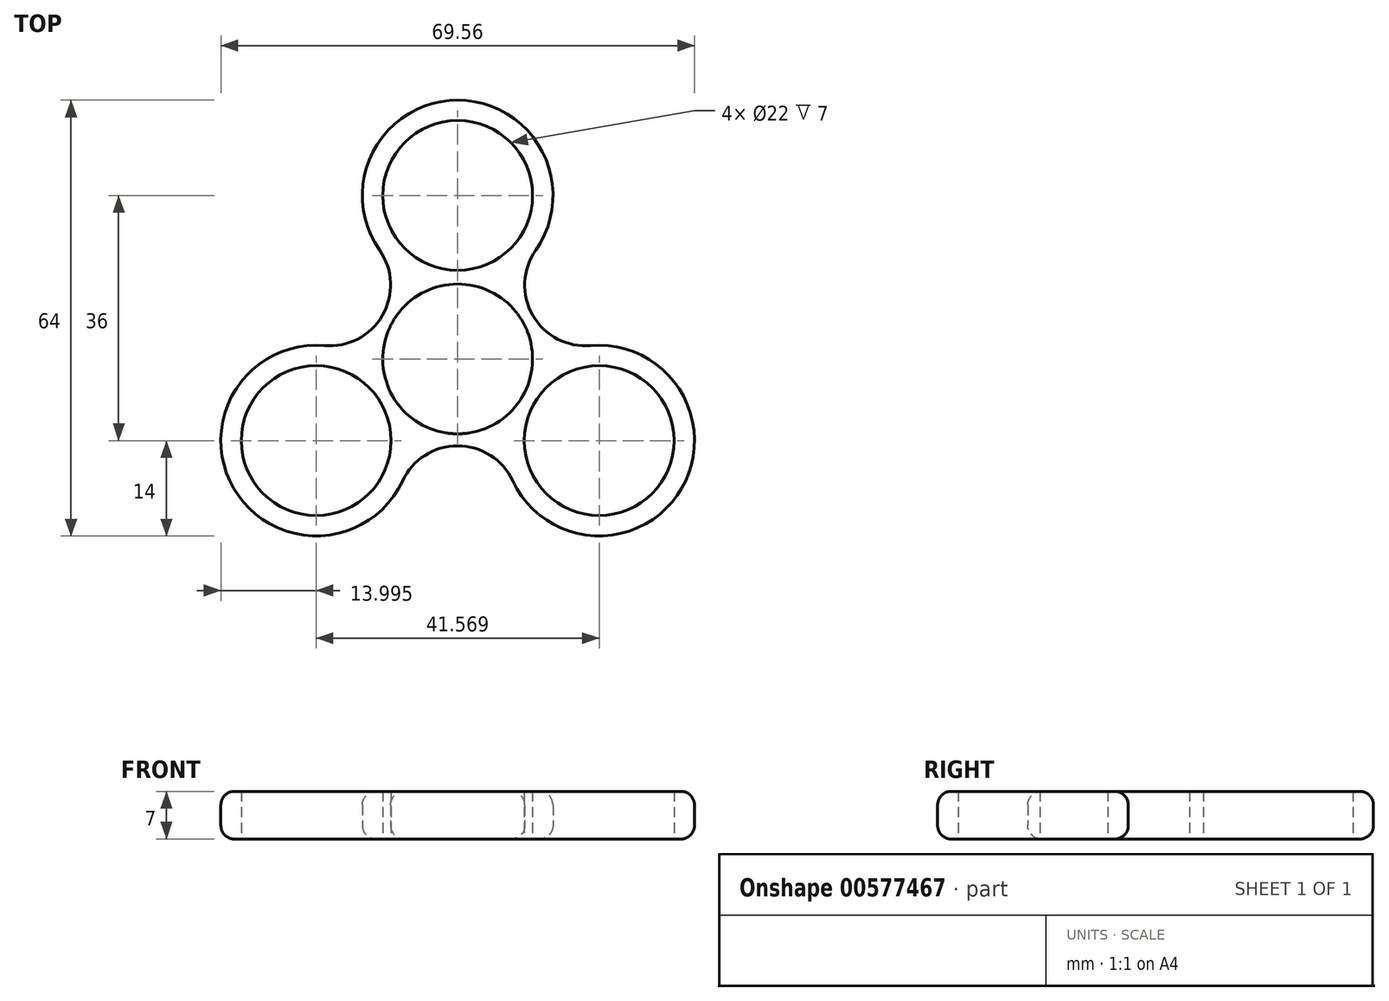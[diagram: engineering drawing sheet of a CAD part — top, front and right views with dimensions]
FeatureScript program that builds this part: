
annotation { "Feature Type Name" : "Feature", "Feature Type Description" : "" }
export const myFeature = defineFeature(function(context is Context, id is Id, definition is map)
    precondition{}
    {
        {
            var Q0;
            Q0=qCreatedBy(makeId("Top.planeOp"),FACE);
            var sketch = newSketch(context, id + "F0", { "sketchPlane" : qUnion([Q0])});
            skCircle(sketch, "E0", {"center": v(0, 0) * mm, "radius": 11 * mm});
            skLineSegment(sketch, "E1", {"start": v(0, 0) * mm, "end": v(0, 11) * mm});
            skCircle(sketch, "E2", {"center": v(0, 24) * mm, "radius": 11 * mm});
            skArc(sketch, "E3.0", {"start": v(11.47, 15.97) * mm, "mid": v(0, 38) * mm, "end": v(-11.47, 15.97) * mm});
            skPoint(sketch, "E4", {"position": v(0, 11) * mm});
            skPoint(sketch, "E5", {"position": v(-12.12, 17) * mm});
            skPoint(sketch, "E6", {"position": v(13, 19.5) * mm});
            skArc(sketch, "E7.1.0", {"start": v(-19.56, 1.95) * mm, "mid": v(-32.9, -19) * mm, "end": v(-8.1, -17.92) * mm});
            skCircle(sketch, "E7.1.1", {"center": v(-20.78, -12) * mm, "radius": 11 * mm});
            skArc(sketch, "E7.2.0", {"start": v(8.1, -17.92) * mm, "mid": v(32.9, -19) * mm, "end": v(19.56, 1.95) * mm});
            skCircle(sketch, "E7.2.1", {"center": v(20.78, -12) * mm, "radius": 11 * mm});
            skPoint(sketch, "E8.1.0", {"position": v(-8.66, -19) * mm});
            skPoint(sketch, "E8.2.0", {"position": v(20.78, 2) * mm});
            skPoint(sketch, "E9.MirrorP", {"position": v(12.12, 17) * mm});
            skPoint(sketch, "E10.1.0", {"position": v(-20.78, 2) * mm});
            skPoint(sketch, "E10.2.0", {"position": v(8.66, -19) * mm});
            skLineSegment(sketch, "E11", {"start": v(-11.05, 6.38) * mm, "end": v(-11.26, 6.5) * mm});
            skPoint(sketch, "E12", {"position": v(-11.26, 6.5) * mm});
            skLineSegment(sketch, "E13", {"start": v(0, 24) * mm, "end": v(-9.01, 17.7) * mm});
            skLineSegment(sketch, "E14.MirrorCS", {"start": v(-20.78, -12) * mm, "end": v(-19.83, -1.04) * mm});
            skPoint(sketch, "E15.orphan", {"position": v(-3.47, 10.44) * mm});
            skArc(sketch, "E16", {"start": v(-11.47, 15.97) * mm, "mid": v(-11.05, 6.38) * mm, "end": v(-19.56, 1.95) * mm});
            skArc(sketch, "E17.1.0", {"start": v(-8.1, -17.92) * mm, "mid": v(0, -12.76) * mm, "end": v(8.1, -17.92) * mm});
            skArc(sketch, "E17.2.0", {"start": v(19.56, 1.95) * mm, "mid": v(11.05, 6.38) * mm, "end": v(11.47, 15.97) * mm});
            skPoint(sketch, "E18.orphan", {"position": v(-10.78, -2.21) * mm});
            skPoint(sketch, "E19.orphan", {"position": v(3.47, 10.44) * mm});
            skPoint(sketch, "E20.orphan", {"position": v(10.78, -2.21) * mm});
            skPoint(sketch, "E21.orphan", {"position": v(7.3, -8.23) * mm});
            skPoint(sketch, "E22.orphan", {"position": v(-7.3, -8.23) * mm});
            skLineSegment(sketch, "E23.trimOffspring", {"start": v(0, 13) * mm, "end": v(0, 24) * mm});
            skSolve(sketch);
        }
        {
            var Q0;
            Q0=makeQuery(id+"F0.imprint","IMPRINT",FACE,{"disambiguationData":[TD([[makeQuery(id+"F0.imprint","IMPRINT",EDGE,{"derivedFrom":sQuery(id+"F0.wireOp",EDGE,"E0")}),-1.0]])]});
            var Q1;
            Q1=makeQuery(id+"F0.imprint","IMPRINT",FACE,{"disambiguationData":[TD([[makeQuery(id+"F0.imprint","IMPRINT",EDGE,{"derivedFrom":sQuery(id+"F0.wireOp",EDGE,"E2")}),-1.0]])]});
            var Q2;
            Q2=makeQuery(id+"F0.imprint","IMPRINT",FACE,{"disambiguationData":[TD([[makeQuery(id+"F0.imprint","IMPRINT",EDGE,{"derivedFrom":sQuery(id+"F0.wireOp",EDGE,"fa5e772c-26e7-4415-bcaa-e380382abe9a.1.1")}),-1.0]])]});
            var Q3;
            Q3=makeQuery(id+"F0.imprint","IMPRINT",FACE,{"disambiguationData":[TD([[makeQuery(id+"F0.imprint","IMPRINT",EDGE,{"derivedFrom":sQuery(id+"F0.wireOp",EDGE,"fa5e772c-26e7-4415-bcaa-e380382abe9a.2.1")}),-1.0]])]});
            extrude(context, id + "F1", {"entities" : qUnion([Q0, Q1, Q2, Q3]), "endBound" : BoundingType.SYMMETRIC, "depth" : 7 * mm, "offsetDistance" : 25 * mm});
        }
        {
            var Q0;
            Q0=makeQuery(id+"F1.opExtrude","CAP_EDGE",EDGE,{"disambiguationData":[OSD([sQuery(id+"F0.wireOp",EDGE,"E3.0")])],"isStart":false});
            var Q1;
            Q1=makeQuery(id+"F1.opExtrude","CAP_EDGE",EDGE,{"disambiguationData":[OSD([sQuery(id+"F0.wireOp",EDGE,"fa5e772c-26e7-4415-bcaa-e380382abe9a.1.0")])],"isStart":true});
            var Q2;
            Q2=makeQuery(id+"F1.opExtrude","CAP_EDGE",EDGE,{"disambiguationData":[OSD([sQuery(id+"F0.wireOp",EDGE,"E3.0")])],"isStart":true});
            fillet(context, id + "F2", {"entities" : qUnion([Q0, Q1, Q2]), "radius" : 2 * mm, "tangentPropagation" : true, "allowEdgeOverflow" : false});
        }
    });
